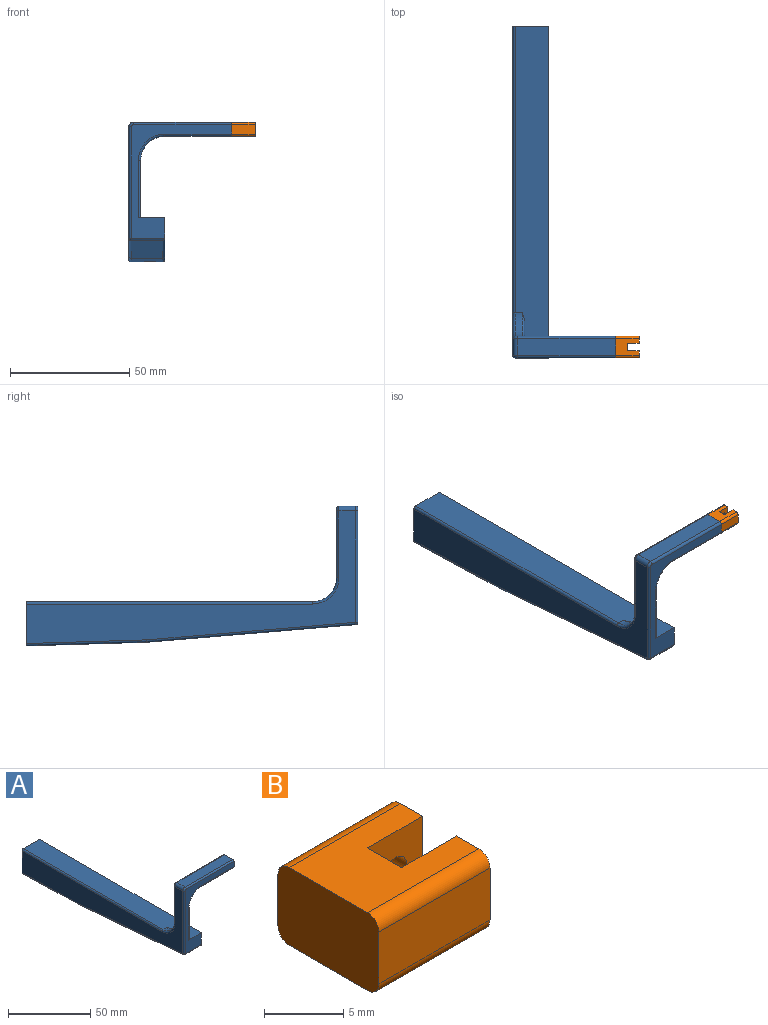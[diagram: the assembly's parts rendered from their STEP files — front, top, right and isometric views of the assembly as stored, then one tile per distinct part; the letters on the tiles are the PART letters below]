
ASSEMBLY  parts=2 mates=1
PART A: 42 faces, bbox 43.2x139.1x58.7 mm
  f0: plane 138x55.52mm, normal (-1,0,0), area 2085.6mm2, adj f8,f19,f22,f23,f24,f31,f33,f37
  f1: plane 50.51x12mm, normal (0,0.03,1), area 589.7mm2, adj f2,f8,f9,f10,f41
  f2: plane 76.49x12mm, normal (0,0.08,1), area 921.2mm2, adj f1,f3,f9,f10
  f3: plane 12x4.56mm, normal (0,1,0), area 54.7mm2, adj f2,f4,f9,f10
  f4: plane 127x12mm, normal (0,0,-1), area 1524mm2, adj f3,f8,f9,f10
  f5: plane 139x14mm, normal (0,0,1), area 1872mm2, adj f8,f9,f12,f16,f18,f24,f28,f40
  f6: plane 87.41x13mm, normal (0,-0.08,-1), area 1140.3mm2, adj f7,f30,f32,f33
  f7: plane 50.68x13mm, normal (0,-0.03,-1), area 642.5mm2, adj f6,f8,f29,f31,f41
  f8: plane 18.53x15.01mm, normal (0,1,0), area 126.9mm2, adj f0,f1,f4,f5,f7,f9,f10,f24
  f9: plane 139x17.52mm, normal (1,0,0), area 744.3mm2, adj f1,f2,f3,f4,f5,f8,f16,f29
  f10: plane 127x12.52mm, normal (1,0,0), area 1188.9mm2, adj f1,f2,f3,f4,f8
  f11: plane 42x29mm, normal (0,1,0), area 268.8mm2, adj f14,f18,f20,f21,f22,f25,f26,f27
  f12: plane 24x13.42mm, normal (1,0,0), area 186.1mm2, adj f5,f17,f27,f28,f40
  f13: plane 28x7mm, normal (0,0,-1), area 196mm2, adj f14,f17,f25,f38
  f14: plane 9x6mm, normal (1,0,0), area 53.1mm2, adj f11,f13,f15,f16,f20,f25,f34,f38
  f15: plane 41x7mm, normal (0,0,1), area 287mm2, adj f14,f19,f20,f34
  f16: plane 47.64x42mm, normal (0,-1,0), area 419.7mm2, adj f5,f9,f14,f30,f32,f34,f36,f37
  f17: cylinder r=10mm len=10mm, axis (0,1,0), area 110mm2, adj f12,f13,f26,f39
  f18: cylinder r=10mm len=10mm, axis (1,0,0), area 47.1mm2, adj f5,f11,f23,f28
  f19: cylinder r=2mm len=7mm, axis (0,-1,0), area 22mm2, adj f0,f15,f21,f36
  f20: cylinder r=1mm len=41mm, axis (-1,0,0), area 64.4mm2, adj f11,f14,f15,f21
  f21: torus R=1mm, axis (0,-1,0), area 4mm2, adj f11,f19,f20,f22
  f22: cylinder r=1mm len=28mm, axis (0,0,1), area 44mm2, adj f0,f11,f21,f23
  f23: torus R=11mm, axis (1,0,0), area 25.6mm2, adj f0,f18,f22,f24
  f24: cylinder r=1mm len=120mm, axis (0,-1,0), area 188.5mm2, adj f0,f5,f8,f23
  f25: cylinder r=1mm len=28mm, axis (1,0,0), area 44mm2, adj f11,f13,f14,f26
  f26: torus R=11mm, axis (0,-1,0), area 25.6mm2, adj f11,f17,f25,f27
  f27: cylinder r=1mm len=14mm, axis (0,0,1), area 22mm2, adj f11,f12,f26,f28
  f28: torus R=11mm, axis (-1,0,0), area 21.8mm2, adj f5,f12,f18,f27
  f29: cylinder r=1mm len=50.71mm, axis (0,-1,0.03), area 79.6mm2, adj f7,f8,f9,f30
  f30: cylinder r=1mm len=88.49mm, axis (0,-1,0.08), area 138.8mm2, adj f6,f9,f16,f29,f32
  f31: cylinder r=1mm len=50.71mm, axis (0,1,-0.03), area 79.6mm2, adj f0,f7,f8,f33
  f32: cylinder r=1mm len=14mm, axis (1,0,0), area 20.2mm2, adj f6,f16,f30,f35
  f33: cylinder r=1mm len=87.49mm, axis (0,1,-0.08), area 137.8mm2, adj f0,f6,f31,f35
  f34: cylinder r=1mm len=41mm, axis (1,0,0), area 64.4mm2, adj f14,f15,f16,f36
  f35: sphere r=1mm, area 1.5mm2, adj f32,f33,f37
  f36: torus R=1mm, axis (0,-1,0), area 4mm2, adj f16,f19,f34,f37
  f37: cylinder r=1mm len=46.64mm, axis (0,0,-1), area 73.3mm2, adj f0,f16,f35,f36
  f38: cylinder r=1mm len=28mm, axis (-1,0,0), area 44mm2, adj f13,f14,f16,f39
  f39: torus R=11mm, axis (0,-1,0), area 25.6mm2, adj f16,f17,f38,f40
  f40: cylinder r=1mm len=24mm, axis (0,0,-1), area 37.7mm2, adj f5,f12,f16,f39
  f41: cylinder r=2.3mm len=4.69mm, axis (0,0.03,1), area 43.4mm2, adj f1,f7
PART B: 17 faces, bbox 9.9x9x6 mm
  f0: plane 9.9x4mm, normal (0,1,0), area 36.5mm2, adj f1,f7,f10,f14,f16
  f1: plane 9x6mm, normal (-1,0,0), area 53.1mm2, adj f0,f2,f8,f9,f13,f14,f15,f16
  f2: plane 9.9x4mm, normal (0,-1,0), area 39.6mm2, adj f1,f3,f13,f15
  f3: plane 6x2.98mm, normal (1,0,0), area 17.4mm2, adj f2,f4,f8,f9,f13,f15
  f4: plane 6x4.9mm, normal (0,1,0), area 26.3mm2, adj f3,f5,f8,f9,f11
  f5: plane 6x3.05mm, normal (1,0,0), area 18.3mm2, adj f4,f6,f8,f9
  f6: plane 6x4.9mm, normal (0,-1,0), area 26.3mm2, adj f5,f7,f8,f9,f10
  f7: plane 6x2.98mm, normal (1,0,0), area 17.4mm2, adj f0,f6,f8,f9,f14,f16
  f8: plane 9.9x7mm, normal (0,0,-1), area 54.4mm2, adj f1,f3,f4,f5,f6,f7,f15,f16
  f9: plane 9.9x7mm, normal (0,0,1), area 54.4mm2, adj f1,f3,f4,f5,f6,f7,f13,f14
  f10: cylinder r=1mm len=2.98mm, axis (0,1,0), area 18.7mm2, adj f0,f6
  f11: cylinder r=1mm len=2mm, axis (0,1,0), area 12.4mm2, adj f4,f12
  f12: plane 2x2mm, normal (0,1,0), area 3.1mm2, adj f11
  f13: cylinder r=1mm len=9.9mm, axis (1,0,0), area 15.6mm2, adj f1,f2,f3,f9
  f14: cylinder r=1mm len=9.9mm, axis (-1,0,0), area 15.6mm2, adj f0,f1,f7,f9
  f15: cylinder r=1mm len=9.9mm, axis (-1,0,0), area 15.6mm2, adj f1,f2,f3,f8
  f16: cylinder r=1mm len=9.9mm, axis (1,0,0), area 15.6mm2, adj f0,f1,f7,f8
PLACE A at identity fixed
PLACE B t=(57.42,-94.33,43.5)mm
MATE fastened A.f14 <-> B.f1  axis (1,0,0) through (40,-134,40.5)mm
